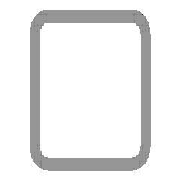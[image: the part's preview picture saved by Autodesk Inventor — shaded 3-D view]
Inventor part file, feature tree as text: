
AUTODESK INVENTOR PART (.ipt)
format: ipt  version: 2016 (Build 200138000, 138)  size: 129,024 bytes
history: native  units: mm (DEFAULTED — no unit token found)
features: other x4, sketch x3, plane x1
ambient origin geometry x8: Origin, YZ Plane, XZ Plane, XY Plane, X Axis, Y Axis, Z Axis, Center Point
bodies: Solid1 (feature_tree), Body (feature_tree)
feature tree (8):
  parser-record x1  (decoder bookkeeping rows leaked as tree rows — omitted from the tree; the rows remain in map.json)
  other  "Driven Length"
  other  "Start plane"
  other  "End plane"
  sketch  "Sketch"  dims[d7=4.0mm d9=60.0mm d11=60.0mm d12=2.0mm d13=-0.0mm d14=463.182711mm d15=30.0mm d16=30.0mm d17=90.0deg d18=463.182711mm]
  sketch  "Sketch3"  dims[d3=463.182711mm]
  plane  "Work Plane3"
  sketch  "Sketch4"  dims[d4=0.0mm]
